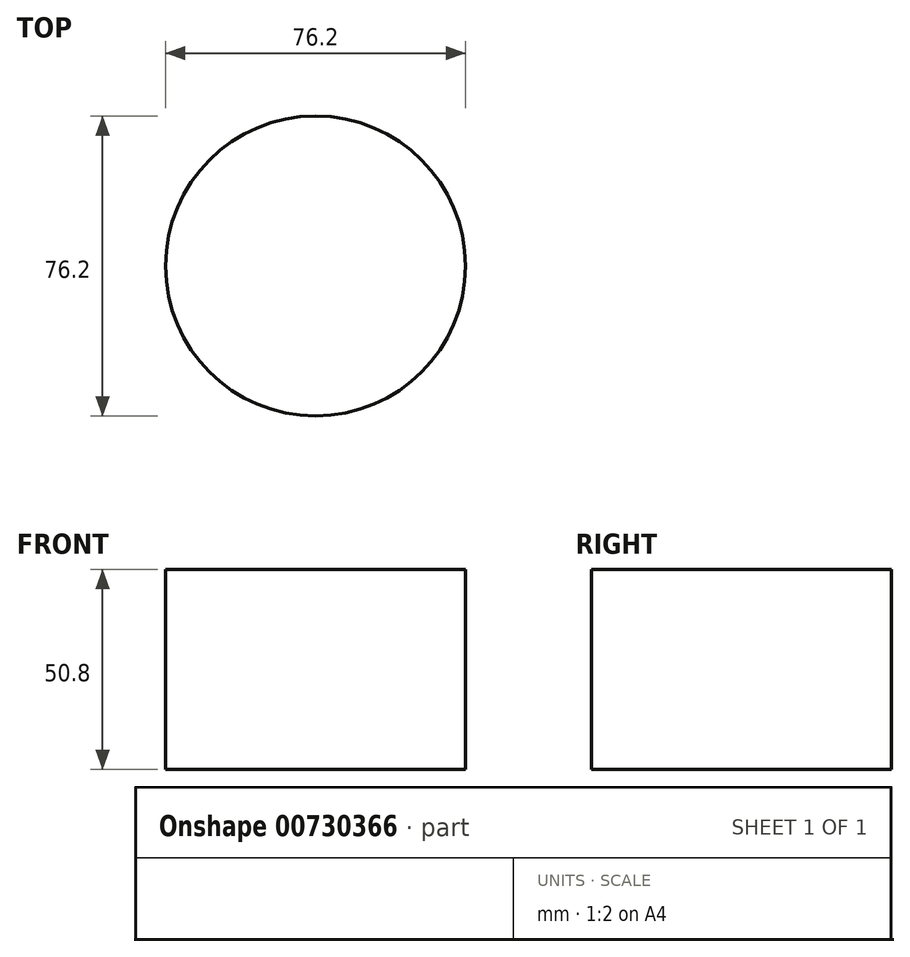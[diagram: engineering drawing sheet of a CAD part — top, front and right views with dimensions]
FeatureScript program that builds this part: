
annotation { "Feature Type Name" : "Feature", "Feature Type Description" : "" }
export const myFeature = defineFeature(function(context is Context, id is Id, definition is map)
    precondition{}
    {
        {
            var Q0;
            Q0=qCreatedBy(makeId("Top.planeOp"),FACE);
            var sketch = newSketch(context, id + "F0", { "sketchPlane" : qUnion([Q0])});
            skCircle(sketch, "E0", {"center": v(-13.36, 34.7) * mm, "radius": 38.1 * mm});
            skSolve(sketch);
        }
        {
            var Q0;
            Q0 = qSketchRegion(id + "F0", true);
            extrude(context, id + "F1", {"entities" : qUnion([Q0]), "depth" : 50.8 * mm, "offsetDistance" : 25.4 * mm});
        }
    });
